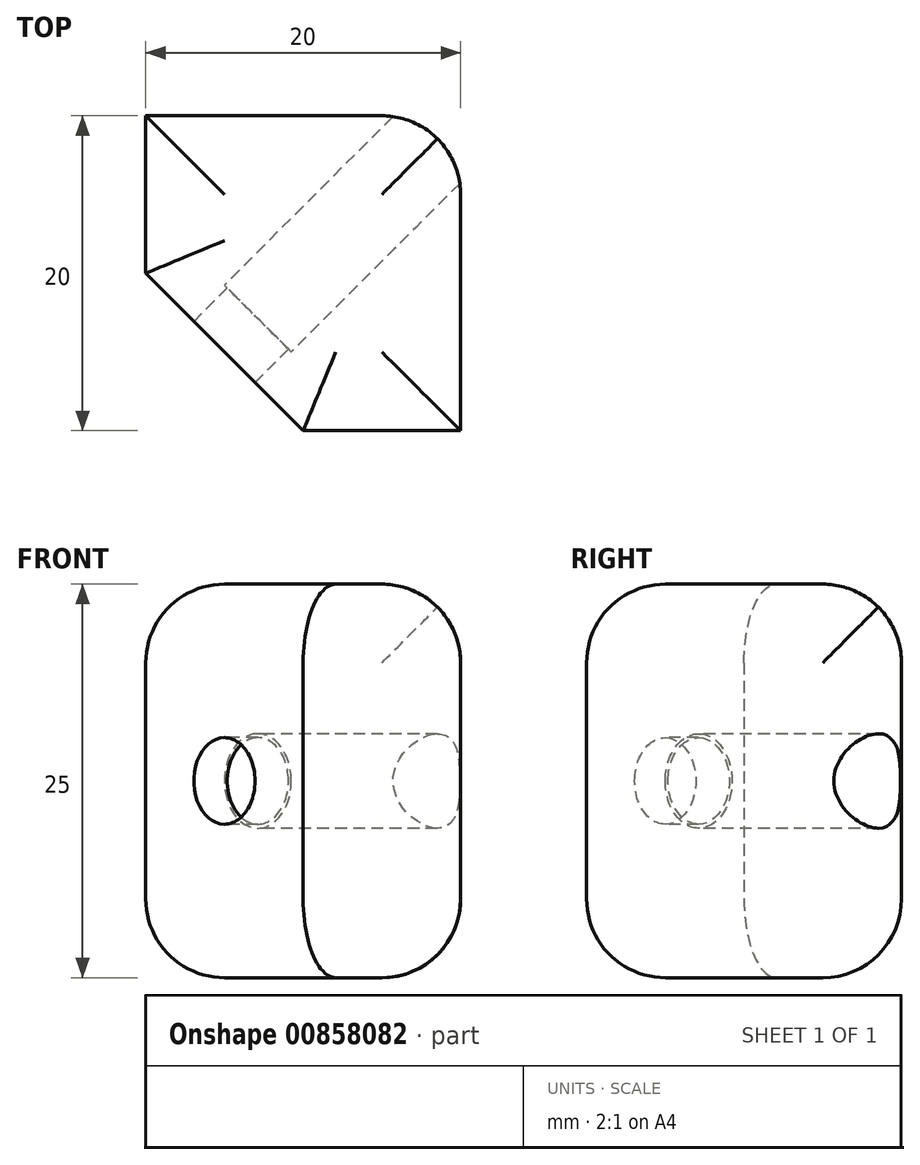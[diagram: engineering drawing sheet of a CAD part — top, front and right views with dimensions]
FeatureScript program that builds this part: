
annotation { "Feature Type Name" : "Feature", "Feature Type Description" : "" }
export const myFeature = defineFeature(function(context is Context, id is Id, definition is map)
    precondition{}
    {
        {
            var Q0;
            Q0=qCreatedBy(makeId("Top.planeOp"),FACE);
            var sketch = newSketch(context, id + "F0", { "sketchPlane" : qUnion([Q0])});
            skLineSegment(sketch, "E0", {"start": v(0, 0) * mm, "end": v(0, -20) * mm});
            skLineSegment(sketch, "E1", {"start": v(-20, 0) * mm, "end": v(0, 0) * mm});
            skLineSegment(sketch, "E2", {"start": v(-20, 0) * mm, "end": v(-20, -10) * mm});
            skLineSegment(sketch, "E3", {"start": v(-20, -10) * mm, "end": v(-10, -20) * mm});
            skLineSegment(sketch, "E4", {"start": v(-10, -20) * mm, "end": v(0, -20) * mm});
            skSolve(sketch);
        }
        {
            var Q0;
            Q0 = qSketchRegion(id + "F0", true);
            extrude(context, id + "F1", {"entities" : qUnion([Q0]), "depth" : 25 * mm, "offsetDistance" : 25 * mm});
        }
        {
            var Q0;
            Q0=makeQuery(id+"F1.opExtrude","SWEPT_FACE",FACE,{"disambiguationData":[OSD([sQuery(id+"F0.wireOp",EDGE,"E3")])]});
            var sketch = newSketch(context, id + "F2", { "sketchPlane" : qUnion([Q0])});
            skCircle(sketch, "E5", {"center": v(0, 12.5) * mm, "radius": 2.75 * mm});
            skPoint(sketch, "E5.centerSnap0", {"position": v(-7.07, 12.5) * mm});
            skSolve(sketch);
        }
        {
            var Q0;
            Q0 = qSketchRegion(id + "F2", true);
            extrude(context, id + "F3", {"entities" : qUnion([Q0]), "operationType" : NewBodyOperationType.REMOVE, "oppositeDirection" : true, "depth" : 25 * mm, "offsetDistance" : 25 * mm});
        }
        {
            var Q0;
            Q0=makeQuery(id+"F1.opExtrude","SWEPT_FACE",FACE,{"disambiguationData":[OSD([sQuery(id+"F0.wireOp",EDGE,"E3")])]});
            cPlane(context, id + "F4", {"entities" : qUnion([Q0]), "cplaneType" : CPlaneType.OFFSET, "offset" : 3 * mm, "oppositeDirection" : true, "width" : 150 * mm, "height" : 150 * mm});
        }
        {
            var Q0;
            Q0=qCreatedBy(id+"F4.planeOp",FACE);
            var sketch = newSketch(context, id + "F5", { "sketchPlane" : qUnion([Q0])});
            skCircle(sketch, "E6", {"center": v(0, 12.5) * mm, "radius": 3 * mm});
            skSolve(sketch);
        }
        {
            var Q0;
            Q0 = qSketchRegion(id + "F5", true);
            extrude(context, id + "F6", {"entities" : qUnion([Q0]), "operationType" : NewBodyOperationType.REMOVE, "oppositeDirection" : true, "depth" : 25 * mm, "offsetDistance" : 25 * mm});
        }
        {
            var Q0;
            Q0=makeQuery(id+"F1.opExtrude","CAP_FACE",FACE,{"disambiguationData":[OSD([sQuery(id+"F0.wireOp",EDGE,"E0"),sQuery(id+"F0.wireOp",EDGE,"E1"),sQuery(id+"F0.wireOp",EDGE,"E2"),sQuery(id+"F0.wireOp",EDGE,"E3"),sQuery(id+"F0.wireOp",EDGE,"E4")])],"isStart":false});
            var Q1;
            Q1=makeQuery(id+"F1.opExtrude","CAP_FACE",FACE,{"disambiguationData":[OSD([sQuery(id+"F0.wireOp",EDGE,"E0"),sQuery(id+"F0.wireOp",EDGE,"E1"),sQuery(id+"F0.wireOp",EDGE,"E2"),sQuery(id+"F0.wireOp",EDGE,"E3"),sQuery(id+"F0.wireOp",EDGE,"E4")])],"isStart":true});
            var Q2;
            {var subQ0=sQuery(id+"F0.wireOp",EDGE,"E0");var subQ1=sQuery(id+"F0.wireOp",EDGE,"E1");Q2=makeQuery(id+"F3.boolean.opBoolean","SPLIT",EDGE,{"disambiguationData":[TD([makeQuery(id+"F1.opExtrude","CAP_FACE",FACE,{"disambiguationData":[OSD([subQ0,subQ1,sQuery(id+"F0.wireOp",EDGE,"E2"),sQuery(id+"F0.wireOp",EDGE,"E3"),sQuery(id+"F0.wireOp",EDGE,"E4")])],"isStart":true})])],"derivedFrom":makeQuery(id+"F1.opExtrude","SWEPT_EDGE",EDGE,{"disambiguationData":[OSD([subQ0,subQ1])]})});}
            fillet(context, id + "F7", {"entities" : qUnion([Q0, Q1, Q2]), "radius" : 5 * mm, "tangentPropagation" : true, "allowEdgeOverflow" : false});
        }
    });
